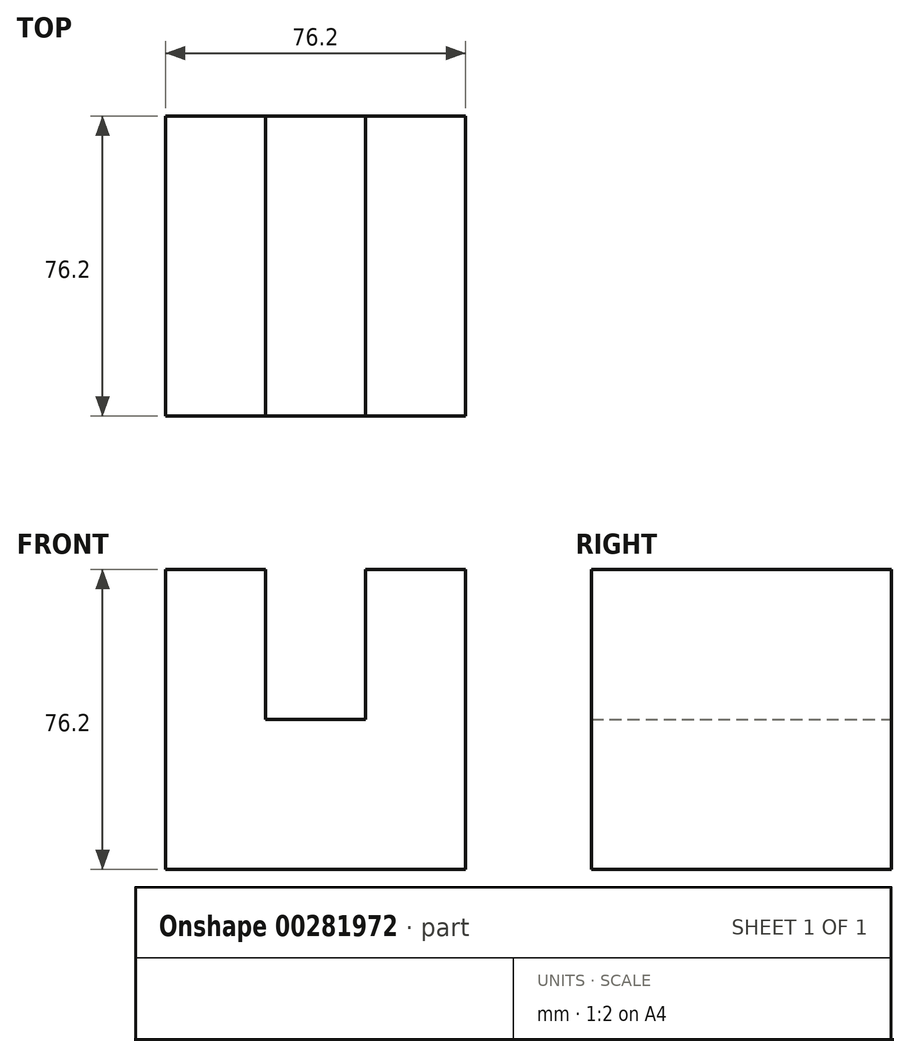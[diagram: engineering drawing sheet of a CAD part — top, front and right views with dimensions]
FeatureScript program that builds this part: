
annotation { "Feature Type Name" : "Feature", "Feature Type Description" : "" }
export const myFeature = defineFeature(function(context is Context, id is Id, definition is map)
    precondition{}
    {
        {
            var Q0;
            Q0=qCreatedBy(makeId("Front.planeOp"),FACE);
            var sketch = newSketch(context, id + "F0", { "sketchPlane" : qUnion([Q0])});
            skLineSegment(sketch, "E0", {"start": v(-61.87, 102.74) * mm, "end": v(-61.87, 26.54) * mm});
            skLineSegment(sketch, "E1", {"start": v(-61.87, 26.54) * mm, "end": v(14.33, 26.54) * mm});
            skLineSegment(sketch, "E2", {"start": v(14.33, 26.54) * mm, "end": v(14.33, 102.74) * mm});
            skLineSegment(sketch, "E3", {"start": v(14.33, 102.74) * mm, "end": v(-11.07, 102.74) * mm});
            skLineSegment(sketch, "E4", {"start": v(-11.07, 102.74) * mm, "end": v(-11.07, 64.64) * mm});
            skLineSegment(sketch, "E5", {"start": v(-11.07, 64.64) * mm, "end": v(-36.47, 64.64) * mm});
            skLineSegment(sketch, "E6", {"start": v(-36.47, 64.64) * mm, "end": v(-36.47, 90.04) * mm});
            skLineSegment(sketch, "E7", {"start": v(-36.47, 90.04) * mm, "end": v(-36.47, 102.74) * mm});
            skLineSegment(sketch, "E8", {"start": v(-36.47, 102.74) * mm, "end": v(-61.87, 102.74) * mm});
            skSolve(sketch);
        }
        {
            var Q0;
            Q0=makeQuery(id+"F0.imprint","IMPRINT",FACE,{"disambiguationData":[TD([[makeQuery(id+"F0.imprint","IMPRINT",EDGE,{"derivedFrom":sQuery(id+"F0.wireOp",EDGE,"E0")}),1.0]])]});
            extrude(context, id + "F1", {"entities" : qUnion([Q0]), "depth" : 76.2 * mm});
        }
    });
